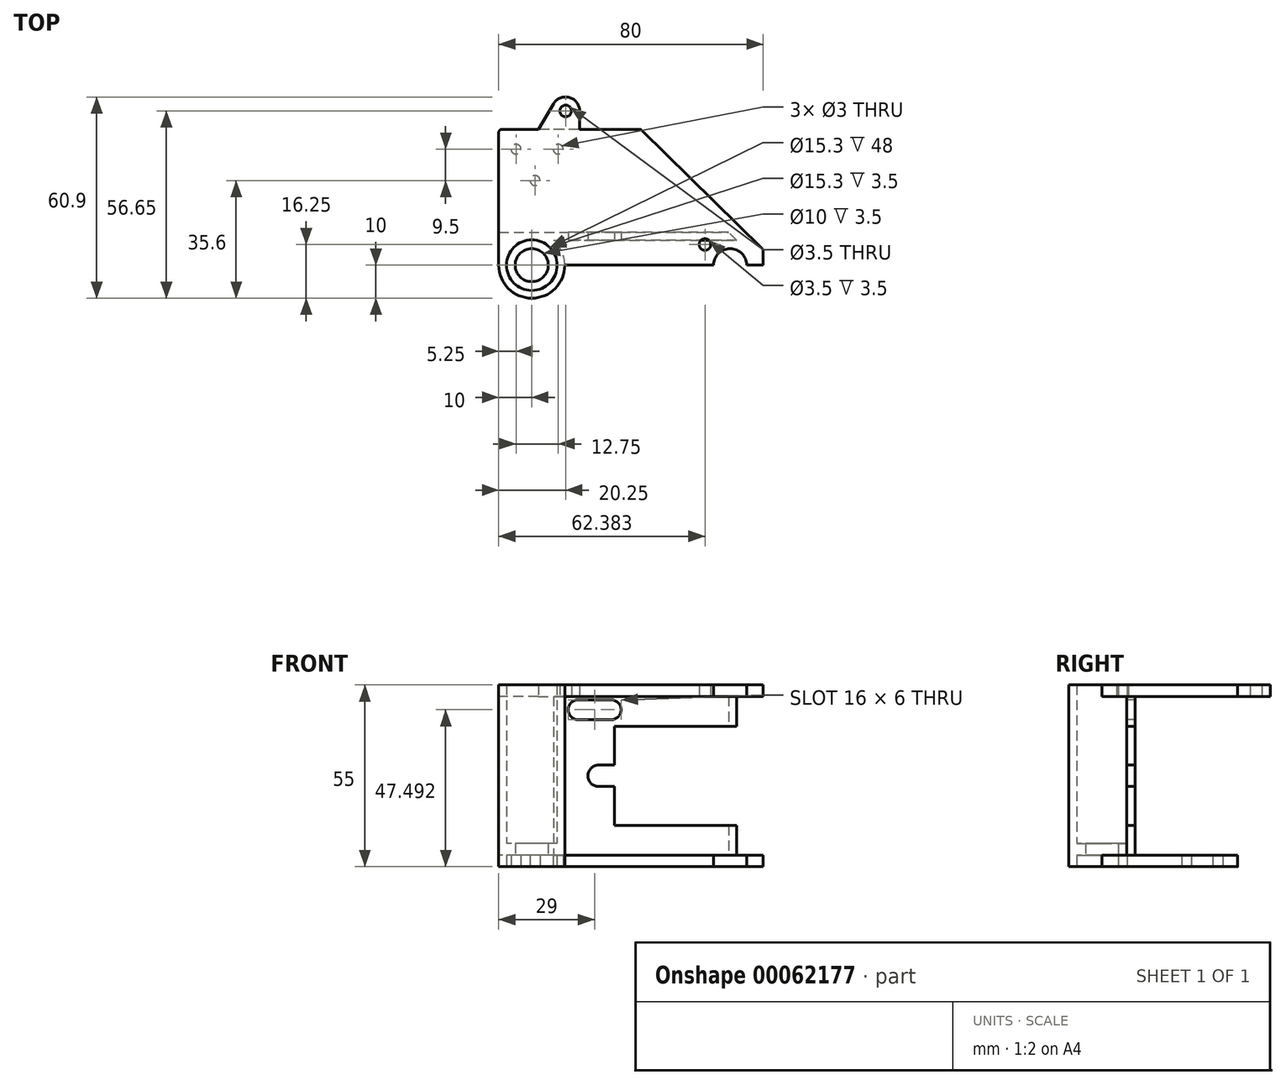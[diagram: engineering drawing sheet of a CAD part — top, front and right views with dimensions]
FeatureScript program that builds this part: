
annotation { "Feature Type Name" : "Feature", "Feature Type Description" : "" }
export const myFeature = defineFeature(function(context is Context, id is Id, definition is map)
    precondition{}
    {
        {
            var Q0;
            Q0=qCreatedBy(makeId("Top.planeOp"),FACE);
            var sketch = newSketch(context, id + "F0", { "sketchPlane" : qUnion([Q0])});
            skLineSegment(sketch, "E0.rect.bottom", {"start": v(21.5, -20.55) * mm, "end": v(-21.5, -20.55) * mm});
            skLineSegment(sketch, "E0.rect.top", {"start": v(21.5, 20.55) * mm, "end": v(-21.5, 20.55) * mm});
            skLineSegment(sketch, "E0.rect.left", {"start": v(21.5, -20.55) * mm, "end": v(21.5, 20.55) * mm});
            skLineSegment(sketch, "E0.rect.right", {"start": v(-21.5, -20.55) * mm, "end": v(-21.5, 20.55) * mm});
            skPoint(sketch, "E0.rect.middle", {"position": v(0, 0) * mm});
            skPoint(sketch, "E1.0.midPoint", {"position": v(21.5, -20.55) * mm});
            skLineSegment(sketch, "E2", {"start": v(21.5, -20.55) * mm, "end": v(43.5, -20.55) * mm});
            skLineSegment(sketch, "E3", {"start": v(58.5, -20.55) * mm, "end": v(58.5, -15.85) * mm});
            skLineSegment(sketch, "E4", {"start": v(58.5, -15.85) * mm, "end": v(21.5, 20.55) * mm});
            skCircle(sketch, "E5", {"center": v(-11.5, -20.55) * mm, "radius": 10 * mm});
            skCircle(sketch, "E6", {"center": v(-11.5, -20.55) * mm, "radius": 7.65 * mm});
            skArc(sketch, "E7", {"start": v(53.5, -20.55) * mm, "mid": v(48.5, -15.55) * mm, "end": v(43.5, -20.55) * mm});
            skLineSegment(sketch, "E8.trimOffspring", {"start": v(53.5, -20.55) * mm, "end": v(58.5, -20.55) * mm});
            skCircle(sketch, "E9", {"center": v(-16.25, 14.55) * mm, "radius": 1.5 * mm});
            skCircle(sketch, "E10", {"center": v(-3.5, 14.55) * mm, "radius": 1.5 * mm});
            skCircle(sketch, "E11", {"center": v(-10.5, 5.05) * mm, "radius": 1.5 * mm});
            skLineSegment(sketch, "E12", {"start": v(-1.5, -20.55) * mm, "end": v(-1.5, 20.55) * mm, "construction": true});
            skSolve(sketch);
        }
        {
            var Q0;
            Q0 = qSketchRegion(id + "F0", true);
            extrude(context, id + "F1", {"entities" : qUnion([Q0]), "depth" : 3.5 * mm});
        }
        {
            var Q0;
            Q0=makeQuery(id+"F1.opExtrude","CAP_FACE",FACE,{"disambiguationData":[OSD([sQuery(id+"F0.wireOp",EDGE,"E0.rect.bottom"),sQuery(id+"F0.wireOp",EDGE,"E0.rect.top"),sQuery(id+"F0.wireOp",EDGE,"E0.rect.right"),sQuery(id+"F0.wireOp",EDGE,"E2"),sQuery(id+"F0.wireOp",EDGE,"E3"),sQuery(id+"F0.wireOp",EDGE,"E4"),sQuery(id+"F0.wireOp",EDGE,"E5"),sQuery(id+"F0.wireOp",EDGE,"E6")])],"isStart":false});
            var sketch = newSketch(context, id + "F2", { "sketchPlane" : qUnion([Q0])});
            skCircle(sketch, "E13", {"center": v(-11.5, -20.55) * mm, "radius": 5 * mm});
            skSolve(sketch);
        }
        {
            var Q0;
            Q0=makeQuery(id+"F1.opExtrude","CAP_FACE",FACE,{"disambiguationData":[OSD([sQuery(id+"F0.wireOp",EDGE,"E0.rect.bottom"),sQuery(id+"F0.wireOp",EDGE,"E0.rect.top"),sQuery(id+"F0.wireOp",EDGE,"E0.rect.right"),sQuery(id+"F0.wireOp",EDGE,"E2"),sQuery(id+"F0.wireOp",EDGE,"E3"),sQuery(id+"F0.wireOp",EDGE,"E4"),sQuery(id+"F0.wireOp",EDGE,"E5"),sQuery(id+"F0.wireOp",EDGE,"E6"),sQuery(id+"F0.wireOp",EDGE,"E7"),sQuery(id+"F0.wireOp",EDGE,"E8.trimOffspring")])],"isStart":false});
            var sketch = newSketch(context, id + "F3", { "sketchPlane" : qUnion([Q0])});
            skLineSegment(sketch, "E14", {"start": v(-21.5, -13.05) * mm, "end": v(50.66, -13.05) * mm});
            skLineSegment(sketch, "E15", {"start": v(50.66, -13.05) * mm, "end": v(48.12, -10.55) * mm});
            skLineSegment(sketch, "E16", {"start": v(48.12, -10.55) * mm, "end": v(-21.5, -10.55) * mm});
            skLineSegment(sketch, "E17", {"start": v(-21.5, -10.55) * mm, "end": v(-21.5, -13.05) * mm});
            skSolve(sketch);
        }
        {
            var Q0;
            {var subQ0=sQuery(id+"F0.wireOp",EDGE,"E5");var subQ1=sQuery(id+"F0.wireOp",EDGE,"E0.rect.bottom");var subQ2=makeQuery(id+"F0.imprint","INTERSECT",VERTEX,{"derivedFrom":[subQ1,subQ0]});Q0=makeQuery(id+"F0.imprint","IMPRINT",FACE,{"disambiguationData":[TD([[makeQuery(id+"F0.imprint","IMPRINT",EDGE,{"disambiguationData":[TD([[subQ2,-1.0]])],"derivedFrom":subQ1}),1.0]])]});}
            var Q1;
            {var subQ0=sQuery(id+"F0.wireOp",EDGE,"E5");var subQ1=sQuery(id+"F0.wireOp",EDGE,"E0.rect.bottom");var subQ2=makeQuery(id+"F0.imprint","INTERSECT",VERTEX,{"derivedFrom":[subQ1,subQ0]});Q1=makeQuery(id+"F0.imprint","IMPRINT",FACE,{"disambiguationData":[TD([[makeQuery(id+"F0.imprint","IMPRINT",EDGE,{"disambiguationData":[TD([[subQ2,-1.0]])],"derivedFrom":subQ1}),-1.0]])]});}
            extrude(context, id + "F4", {"entities" : qUnion([Q0, Q1]), "operationType" : NewBodyOperationType.ADD, "depth" : 51.5 * mm});
        }
        {
            var Q0;
            Q0=makeQuery(id+"F2.imprint","IMPRINT",FACE,{"disambiguationData":[TD([[makeQuery(id+"F2.imprint","IMPRINT",EDGE,{"derivedFrom":sQuery(id+"F2.wireOp",EDGE,"E13")}),-1.0]])]});
            extrude(context, id + "F5", {"entities" : qUnion([Q0]), "operationType" : NewBodyOperationType.ADD, "depth" : 3.5 * mm});
        }
        {
            var Q0;
            Q0=sQuery(id+"F3.wireOp",EDGE,"E14");
            cPlane(context, id + "F6", {"entities" : qUnion([Q0]), "cplaneType" : CPlaneType.LINE_ANGLE, "offset" : 0 * mm, "angle" : 0 * degree, "width" : 150 * mm, "height" : 150 * mm});
        }
        {
            var Q0;
            Q0=qCreatedBy(id+"F6.planeOp",FACE);
            var sketch = newSketch(context, id + "F7", { "sketchPlane" : qUnion([Q0])});
            skLineSegment(sketch, "E18.bottom", {"start": v(21.5, 3.5) * mm, "end": v(-50.5, 3.5) * mm});
            skLineSegment(sketch, "E18.top", {"start": v(21.5, 51.5) * mm, "end": v(-50.5, 51.5) * mm});
            skLineSegment(sketch, "E18.left", {"start": v(21.5, 3.5) * mm, "end": v(21.5, 51.5) * mm});
            skLineSegment(sketch, "E18.right", {"start": v(-50.5, 3.5) * mm, "end": v(-50.5, 12.5) * mm});
            skLineSegment(sketch, "E19.bottom", {"start": v(-50.5, 42.5) * mm, "end": v(-13.5, 42.5) * mm});
            skLineSegment(sketch, "E19.top", {"start": v(-50.5, 12.5) * mm, "end": v(-13.5, 12.5) * mm});
            skLineSegment(sketch, "E19.right", {"start": v(-13.5, 42.5) * mm, "end": v(-13.5, 30.75) * mm});
            skLineSegment(sketch, "E20.trimOffspring", {"start": v(-50.5, 42.5) * mm, "end": v(-50.5, 51.5) * mm});
            skLineSegment(sketch, "E21.bottom", {"start": v(-13.5, 30.75) * mm, "end": v(-8.75, 30.75) * mm});
            skLineSegment(sketch, "E21.top", {"start": v(-13.5, 24.25) * mm, "end": v(-8.75, 24.25) * mm});
            skArc(sketch, "E22", {"start": v(-8.75, 24.25) * mm, "mid": v(-5.5, 27.5) * mm, "end": v(-8.75, 30.75) * mm});
            skLineSegment(sketch, "E23.trimOffspring", {"start": v(-13.5, 24.25) * mm, "end": v(-13.5, 12.5) * mm});
            skLineSegment(sketch, "E24.bottom", {"start": v(-12.5, 50.5) * mm, "end": v(-2.5, 50.5) * mm});
            skLineSegment(sketch, "E24.top", {"start": v(-12.5, 44.5) * mm, "end": v(-2.5, 44.5) * mm});
            skArc(sketch, "E25", {"start": v(-2.5, 44.5) * mm, "mid": v(0.5, 47.5) * mm, "end": v(-2.5, 50.5) * mm});
            skArc(sketch, "E26", {"start": v(-12.5, 50.5) * mm, "mid": v(-15.5, 47.5) * mm, "end": v(-12.5, 44.5) * mm});
            skSolve(sketch);
        }
        {
            var Q0;
            Q0 = qSketchRegion(id + "F7", true);
            extrude(context, id + "F8", {"entities" : qUnion([Q0]), "operationType" : NewBodyOperationType.ADD, "depth" : 2.5 * mm});
        }
        {
            var Q0;
            Q0=makeQuery(id+"F8.opExtrude","CAP_EDGE",EDGE,{"disambiguationData":[OSD([sQuery(id+"F7.wireOp",EDGE,"E18.right")])],"isStart":false});
            var Q1;
            Q1=makeQuery(id+"F8.opExtrude","CAP_EDGE",EDGE,{"disambiguationData":[OSD([sQuery(id+"F7.wireOp",EDGE,"E20.trimOffspring")])],"isStart":false});
            chamfer(context, id + "F9", {"entities" : qUnion([Q0, Q1]), "width" : 2.5 * mm});
        }
        {
            var Q0;
            Q0=makeQuery(id+"F8.boolean.opBoolean","MERGE",FACE,{"derivedFrom":[makeQuery(id+"F4.opExtrude","CAP_FACE",FACE,{"disambiguationData":[OSD([sQuery(id+"F0.wireOp",EDGE,"E5"),sQuery(id+"F0.wireOp",EDGE,"E6")])],"isStart":false}),makeQuery(id+"F8.opExtrude","SWEPT_FACE",FACE,{"disambiguationData":[OSD([sQuery(id+"F7.wireOp",EDGE,"E18.top")])]})]});
            var sketch = newSketch(context, id + "F10", { "sketchPlane" : qUnion([Q0])});
            skLineSegment(sketch, "E27.rect.bottom", {"start": v(21.5, -20.55) * mm, "end": v(-21.5, -20.55) * mm});
            skLineSegment(sketch, "E27.rect.top", {"start": v(21.5, 20.55) * mm, "end": v(-21.5, 20.55) * mm});
            skLineSegment(sketch, "E27.rect.left", {"start": v(21.5, -20.55) * mm, "end": v(21.5, 20.55) * mm});
            skLineSegment(sketch, "E27.rect.right", {"start": v(-21.5, -20.55) * mm, "end": v(-21.5, 20.55) * mm});
            skPoint(sketch, "E27.rect.middle", {"position": v(0, 0) * mm});
            skPoint(sketch, "E28.0.midPoint", {"position": v(21.5, -20.55) * mm});
            skLineSegment(sketch, "E29", {"start": v(21.5, -20.55) * mm, "end": v(43.5, -20.55) * mm});
            skLineSegment(sketch, "E30", {"start": v(58.5, -20.55) * mm, "end": v(58.5, -15.85) * mm});
            skLineSegment(sketch, "E31", {"start": v(58.5, -15.85) * mm, "end": v(21.5, 20.55) * mm});
            skCircle(sketch, "E32", {"center": v(-11.5, -20.55) * mm, "radius": 10 * mm});
            skCircle(sketch, "E33", {"center": v(-11.5, -20.55) * mm, "radius": 7.65 * mm});
            skArc(sketch, "E34", {"start": v(53.5, -20.55) * mm, "mid": v(48.5, -15.55) * mm, "end": v(43.5, -20.55) * mm});
            skLineSegment(sketch, "E35.trimOffspring", {"start": v(53.5, -20.55) * mm, "end": v(58.5, -20.55) * mm});
            skCircle(sketch, "E36", {"center": v(40.88, -14.3) * mm, "radius": 1.75 * mm});
            skLineSegment(sketch, "E37.0", {"start": v(3, 26.1) * mm, "end": v(3, 20.55) * mm});
            skLineSegment(sketch, "E37.1", {"start": v(3, 20.55) * mm, "end": v(-9.5, 20.55) * mm});
            skLineSegment(sketch, "E37.2", {"start": v(-9.5, 20.55) * mm, "end": v(-4.9, 28.27) * mm});
            skCircle(sketch, "E38", {"center": v(-1.25, 26.1) * mm, "radius": 1.75 * mm});
            skPoint(sketch, "E39.visualSharp", {"position": v(3, 41.55) * mm});
            skArc(sketch, "E39.filletArc", {"start": v(3, 26.1) * mm, "mid": v(-0.12, 30.2) * mm, "end": v(-4.9, 28.27) * mm});
            skSolve(sketch);
        }
        {
            var Q0;
            Q0 = qSketchRegion(id + "F10", true);
            extrude(context, id + "F11", {"entities" : qUnion([Q0]), "operationType" : NewBodyOperationType.ADD, "depth" : 3.5 * mm});
        }
        {
            var Q0;
            {var subQ0=sQuery(id+"F7.wireOp",EDGE,"E18.left");var subQ1=sQuery(id+"F0.wireOp",EDGE,"E5");var subQ2=sQuery(id+"F0.wireOp",EDGE,"E0.rect.right");Q0=makeQuery(id+"F8.boolean.opBoolean","SPLIT",FACE,{"disambiguationData":[TD([makeQuery(id+"F1.opExtrude","SWEPT_FACE",FACE,{"disambiguationData":[OSD([subQ2])]}),makeQuery(id+"F1.opExtrude","SWEPT_FACE",FACE,{"disambiguationData":[OSD([subQ1])]}),makeQuery(id+"F4.opExtrude","SWEPT_FACE",FACE,{"disambiguationData":[OSD([subQ1])]}),makeQuery(id+"F8.opExtrude","CAP_FACE",FACE,{"disambiguationData":[OSD([sQuery(id+"F7.wireOp",EDGE,"E18.bottom"),sQuery(id+"F7.wireOp",EDGE,"E18.top"),subQ0,sQuery(id+"F7.wireOp",EDGE,"E18.right"),sQuery(id+"F7.wireOp",EDGE,"E19.bottom"),sQuery(id+"F7.wireOp",EDGE,"E19.top"),sQuery(id+"F7.wireOp",EDGE,"E19.right"),sQuery(id+"F7.wireOp",EDGE,"E20.trimOffspring"),sQuery(id+"F7.wireOp",EDGE,"E21.bottom"),sQuery(id+"F7.wireOp",EDGE,"E21.top"),sQuery(id+"F7.wireOp",EDGE,"E22"),sQuery(id+"F7.wireOp",EDGE,"E23.trimOffspring"),sQuery(id+"F7.wireOp",EDGE,"E24.bottom"),sQuery(id+"F7.wireOp",EDGE,"E24.top"),sQuery(id+"F7.wireOp",EDGE,"E25"),sQuery(id+"F7.wireOp",EDGE,"E26")])],"isStart":true}),makeQuery(id+"F8.opExtrude","SWEPT_FACE",FACE,{"disambiguationData":[OSD([subQ0])]})])],"derivedFrom":makeQuery(id+"F1.opExtrude","CAP_FACE",FACE,{"disambiguationData":[OSD([sQuery(id+"F0.wireOp",EDGE,"E0.rect.bottom"),sQuery(id+"F0.wireOp",EDGE,"E0.rect.top"),subQ2,sQuery(id+"F0.wireOp",EDGE,"E2"),sQuery(id+"F0.wireOp",EDGE,"E3"),sQuery(id+"F0.wireOp",EDGE,"E4"),subQ1,sQuery(id+"F0.wireOp",EDGE,"E6"),sQuery(id+"F0.wireOp",EDGE,"E7"),sQuery(id+"F0.wireOp",EDGE,"E8.trimOffspring"),sQuery(id+"F0.wireOp",EDGE,"E9"),sQuery(id+"F0.wireOp",EDGE,"E10"),sQuery(id+"F0.wireOp",EDGE,"E11")])],"isStart":false})});}
            extrude(context, id + "F12", {"entities" : qUnion([Q0]), "operationType" : NewBodyOperationType.ADD, "depth" : 48 * mm});
        }
        {
            var Q0;
            Q0=makeQuery(id+"F11.opExtrude","SWEPT_EDGE",EDGE,{"disambiguationData":[OSD([sQuery(id+"F10.wireOp",EDGE,"E27.rect.top"),sQuery(id+"F10.wireOp",EDGE,"E27.rect.right")])]});
            var Q1;
            Q1=makeQuery(id+"F11.opExtrude","SWEPT_EDGE",EDGE,{"disambiguationData":[OSD([sQuery(id+"F10.wireOp",EDGE,"E27.rect.top"),sQuery(id+"F10.wireOp",EDGE,"E27.rect.left"),sQuery(id+"F10.wireOp",EDGE,"E31")])]});
            var Q2;
            Q2=makeQuery(id+"F11.opExtrude","SWEPT_EDGE",EDGE,{"disambiguationData":[OSD([sQuery(id+"F10.wireOp",EDGE,"E30"),sQuery(id+"F10.wireOp",EDGE,"E31")])]});
            var Q3;
            Q3=makeQuery(id+"F1.opExtrude","SWEPT_EDGE",EDGE,{"disambiguationData":[OSD([sQuery(id+"F0.wireOp",EDGE,"E3"),sQuery(id+"F0.wireOp",EDGE,"E4")])]});
            var Q4;
            Q4=makeQuery(id+"F1.opExtrude","SWEPT_EDGE",EDGE,{"disambiguationData":[OSD([sQuery(id+"F0.wireOp",EDGE,"E0.rect.top"),sQuery(id+"F0.wireOp",EDGE,"E0.rect.left"),sQuery(id+"F0.wireOp",EDGE,"E4")])]});
            var Q5;
            Q5=makeQuery(id+"F1.opExtrude","SWEPT_EDGE",EDGE,{"disambiguationData":[OSD([sQuery(id+"F0.wireOp",EDGE,"E0.rect.top"),sQuery(id+"F0.wireOp",EDGE,"E0.rect.right")])]});
            fillet(context, id + "F13", {"entities" : qUnion([Q0, Q1, Q2, Q3, Q4, Q5]), "radius" : 1 * mm, "tangentPropagation" : true, "allowEdgeOverflow" : false});
        }
        {
            var Q0;
            Q0=makeQuery(id+"F11.opExtrude","CAP_FACE",FACE,{"disambiguationData":[OSD([sQuery(id+"F10.wireOp",EDGE,"E27.rect.bottom"),sQuery(id+"F10.wireOp",EDGE,"E27.rect.top"),sQuery(id+"F10.wireOp",EDGE,"E27.rect.right"),sQuery(id+"F10.wireOp",EDGE,"E29"),sQuery(id+"F10.wireOp",EDGE,"E30"),sQuery(id+"F10.wireOp",EDGE,"E31"),sQuery(id+"F10.wireOp",EDGE,"E32"),sQuery(id+"F10.wireOp",EDGE,"E33"),sQuery(id+"F10.wireOp",EDGE,"E34"),sQuery(id+"F10.wireOp",EDGE,"E35.trimOffspring"),sQuery(id+"F10.wireOp",EDGE,"E36"),sQuery(id+"F10.wireOp",EDGE,"E37.0"),sQuery(id+"F10.wireOp",EDGE,"E37.2"),sQuery(id+"F10.wireOp",EDGE,"E38"),sQuery(id+"F10.wireOp",EDGE,"E39.filletArc")])],"isStart":false});
            var sketch = newSketch(context, id + "F14", { "sketchPlane" : qUnion([Q0])});
            skCircle(sketch, "E40", {"center": v(-11.5, -20.55) * mm, "radius": 7.65 * mm});
            skPoint(sketch, "E40.first.point", {"position": v(-18.07, -16.63) * mm});
            skPoint(sketch, "E40.second.point", {"position": v(-4.89, -24.4) * mm});
            skPoint(sketch, "E40.third.point", {"position": v(-7.99, -13.75) * mm});
            skSolve(sketch);
        }
        {
            var Q0;
            Q0 = qSketchRegion(id + "F14", true);
            var Q1;
            Q1=makeQuery(id+"F5.opExtrude","CAP_FACE",FACE,{"disambiguationData":[OSD([sQuery(id+"F0.wireOp",EDGE,"E6"),sQuery(id+"F2.wireOp",EDGE,"E13")])],"isStart":false});
            extrude(context, id + "F15", {"entities" : qUnion([Q0]), "operationType" : NewBodyOperationType.REMOVE, "endBound" : BoundingType.UP_TO_SURFACE, "oppositeDirection" : true, "endBoundEntityFace" : qUnion([Q1]), "depth" : 25 * mm});
        }
    });
